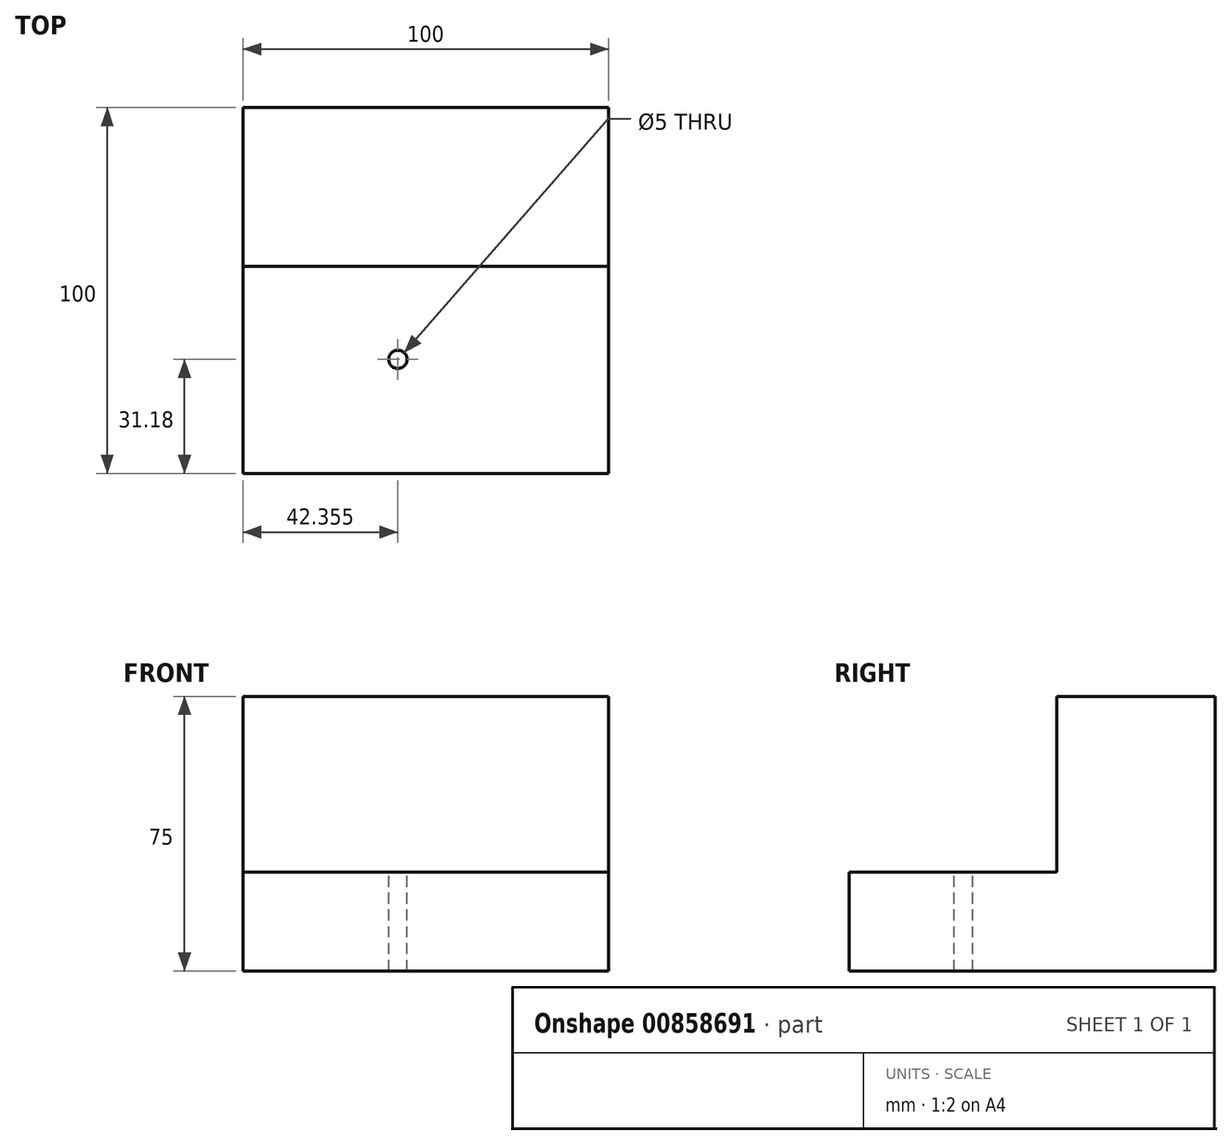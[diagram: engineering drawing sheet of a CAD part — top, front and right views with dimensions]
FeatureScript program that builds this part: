
annotation { "Feature Type Name" : "Feature", "Feature Type Description" : "" }
export const myFeature = defineFeature(function(context is Context, id is Id, definition is map)
    precondition{}
    {
        {
            var Q0;
            Q0=qCreatedBy(makeId("Top.planeOp"),FACE);
            var sketch = newSketch(context, id + "F0", { "sketchPlane" : qUnion([Q0])});
            skLineSegment(sketch, "E0.bottom", {"start": v(-45.53, 68.82) * mm, "end": v(54.47, 68.82) * mm});
            skLineSegment(sketch, "E0.top", {"start": v(-45.53, -31.18) * mm, "end": v(54.47, -31.18) * mm});
            skLineSegment(sketch, "E0.left", {"start": v(-45.53, 68.82) * mm, "end": v(-45.53, -31.18) * mm});
            skLineSegment(sketch, "E0.right", {"start": v(54.47, 68.82) * mm, "end": v(54.47, -31.18) * mm});
            skSolve(sketch);
        }
        {
            var Q0;
            Q0 = qSketchRegion(id + "F0", true);
            extrude(context, id + "F1", {"entities" : qUnion([Q0]), "depth" : 100 * mm, "offsetDistance" : 25 * mm});
        }
        {
            var Q0;
            Q0=makeQuery(id+"F1.opExtrude","CAP_FACE",FACE,{"disambiguationData":[OSD([sQuery(id+"F0.wireOp",EDGE,"E0.bottom"),sQuery(id+"F0.wireOp",EDGE,"E0.top"),sQuery(id+"F0.wireOp",EDGE,"E0.left"),sQuery(id+"F0.wireOp",EDGE,"E0.right")])],"isStart":false});
            var sketch = newSketch(context, id + "F2", { "sketchPlane" : qUnion([Q0])});
            skLineSegment(sketch, "E1.bottom", {"start": v(-60.36, -39) * mm, "end": v(83.52, -39) * mm});
            skLineSegment(sketch, "E1.top", {"start": v(-60.36, 25.48) * mm, "end": v(83.52, 25.48) * mm});
            skLineSegment(sketch, "E1.left", {"start": v(-60.36, -39) * mm, "end": v(-60.36, 25.48) * mm});
            skLineSegment(sketch, "E1.right", {"start": v(83.52, -39) * mm, "end": v(83.52, 25.48) * mm});
            skSolve(sketch);
        }
        {
            var Q0;
            Q0 = qSketchRegion(id + "F2", true);
            extrude(context, id + "F3", {"entities" : qUnion([Q0]), "operationType" : NewBodyOperationType.REMOVE, "oppositeDirection" : true, "depth" : 48 * mm, "offsetDistance" : 25 * mm});
        }
        {
            var Q0;
            Q0=makeQuery(id+"F3.boolean.opBoolean","COPY",FACE,{"derivedFrom":makeQuery(id+"F3.opExtrude","CAP_FACE",FACE,{"disambiguationData":[OSD([sQuery(id+"F2.wireOp",EDGE,"E1.bottom"),sQuery(id+"F2.wireOp",EDGE,"E1.top"),sQuery(id+"F2.wireOp",EDGE,"E1.left"),sQuery(id+"F2.wireOp",EDGE,"E1.right")])],"isStart":false})});
            var sketch = newSketch(context, id + "F4", { "sketchPlane" : qUnion([Q0])});
            skCircle(sketch, "E2", {"center": v(-3.18, 0) * mm, "radius": 2.5 * mm});
            skSolve(sketch);
        }
        {
            var Q0;
            Q0 = qSketchRegion(id + "F4", true);
            extrude(context, id + "F5", {"entities" : qUnion([Q0]), "operationType" : NewBodyOperationType.REMOVE, "endBound" : BoundingType.THROUGH_ALL, "oppositeDirection" : true, "depth" : 25 * mm, "offsetDistance" : 25 * mm});
        }
        {
            var Q0;
            Q0=makeQuery(id+"F1.opExtrude","CAP_FACE",FACE,{"disambiguationData":[OSD([sQuery(id+"F0.wireOp",EDGE,"E0.bottom"),sQuery(id+"F0.wireOp",EDGE,"E0.top"),sQuery(id+"F0.wireOp",EDGE,"E0.left"),sQuery(id+"F0.wireOp",EDGE,"E0.right")])],"isStart":true});
            var sketch = newSketch(context, id + "F6", { "sketchPlane" : qUnion([Q0])});
            skLineSegment(sketch, "E3.bottom", {"start": v(65.82, 43.23) * mm, "end": v(-58.78, 43.23) * mm});
            skLineSegment(sketch, "E3.top", {"start": v(65.82, -78.8) * mm, "end": v(-58.78, -78.8) * mm});
            skLineSegment(sketch, "E3.left", {"start": v(65.82, 43.23) * mm, "end": v(65.82, -78.8) * mm});
            skLineSegment(sketch, "E3.right", {"start": v(-58.78, 43.23) * mm, "end": v(-58.78, -78.8) * mm});
            skSolve(sketch);
        }
        {
            var Q0;
            Q0 = qSketchRegion(id + "F6", true);
            extrude(context, id + "F7", {"entities" : qUnion([Q0]), "operationType" : NewBodyOperationType.REMOVE, "oppositeDirection" : true, "depth" : 25 * mm, "offsetDistance" : 25 * mm});
        }
    });
